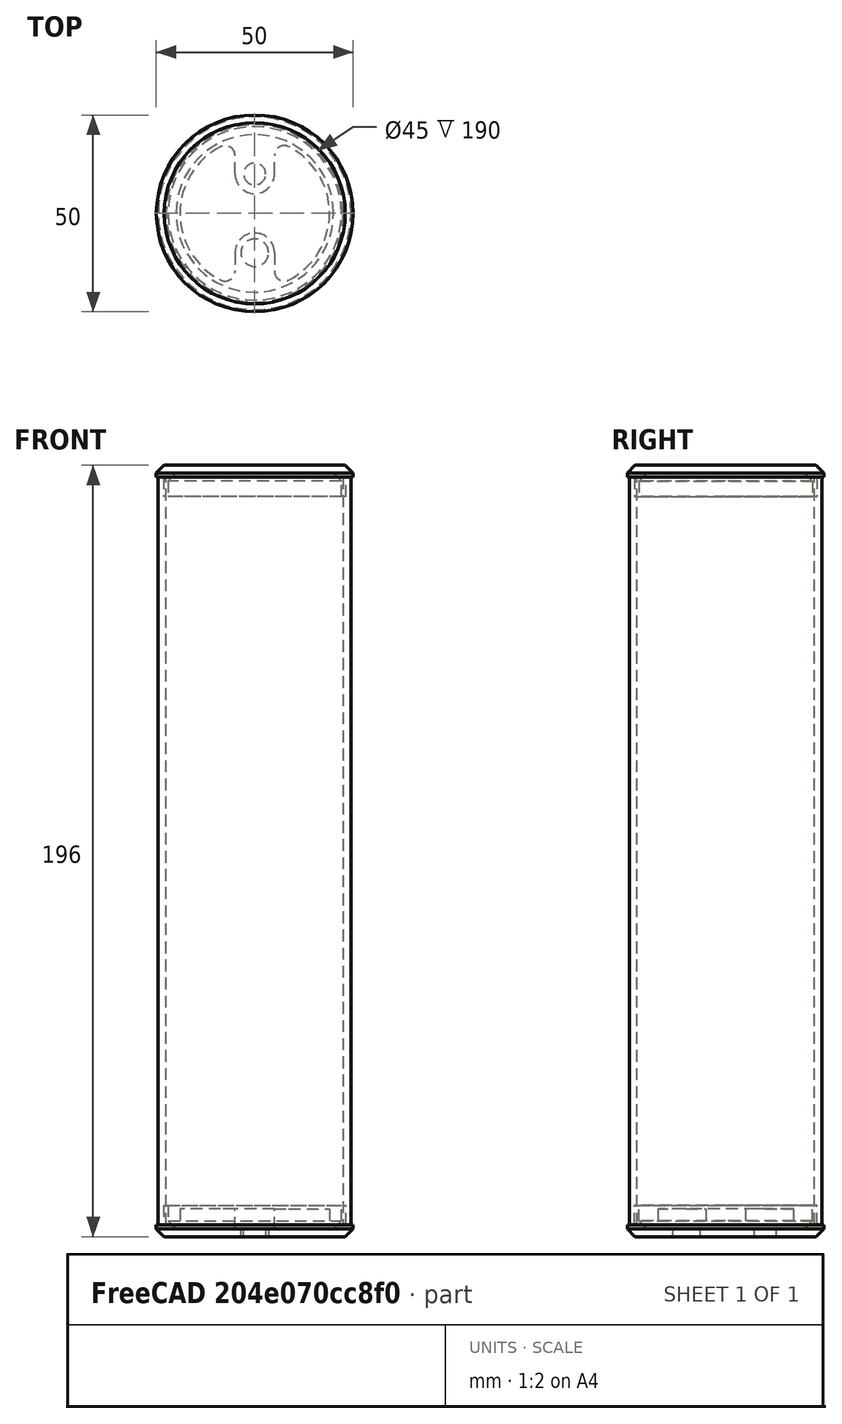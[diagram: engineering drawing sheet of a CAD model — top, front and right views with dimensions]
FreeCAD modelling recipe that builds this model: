
FCSTD DOCUMENT  (FreeCAD 0.19R14555 (Git shallow))
Label: hydrostatus_mockup
License: All rights reserved
LicenseURL: http://en.wikipedia.org/wiki/All_rights_reserved
objects: TechDraw::DrawViewDimension×13, Sketcher::SketchObject×9, PartDesign::Pad×6, TechDraw::DrawViewPart×6, PartDesign::Chamfer×4, PartDesign::Body×4, PartDesign::Pocket×3, Mesh::Feature×1, TechDraw::DrawSVGTemplate×1, TechDraw::DrawPage×1
note: 39 computed .brp shape members not serialized (recipe doc carries the construction recipe); baked Part::Feature solids carry a one-line shape summary decoded from their .brp

FEATURE [Sketcher::SketchObject] Sketch
  FullyConstrained = true
  MapMode = 5
  Support = -> [XY_Plane]
  sketch-geometry (1):
    g0: Circle CenterX=0 CenterY=0 CenterZ=0 NormalX=0 NormalY=0 NormalZ=1 AngleXU=0 Radius=23.15
  constraints (2):
    c: Coincident(g0,g-1)
    c: Diameter(g0) = 46.3
FEATURE [PartDesign::Pad] Pad
  Direction = (1,1,1)
  Length = 5
  Length2 = 100
  Profile = -> Sketch
  Type = 0
FEATURE [Sketcher::SketchObject] Sketch001
  FullyConstrained = true
  MapMode = 5
  Placement = pos=(0,0,5) rot=(0,0,1;0rad)
  Support = -> [Pad]
  sketch-geometry (1):
    g0: Circle CenterX=0 CenterY=0 CenterZ=0 NormalX=0 NormalY=0 NormalZ=1 AngleXU=0 Radius=25
  constraints (2):
    c: Coincident(g0,g-1)
    c: Diameter(g0) = 50
FEATURE [PartDesign::Pad] Pad001
  BaseFeature = -> Pad
  Direction = (1,1,1)
  Length = 3
  Length2 = 100
  Profile = -> Sketch001
  Type = 0
FEATURE [PartDesign::Chamfer] Chamfer
  Angle = 45
  Base = -> Pad001 [Edge3]
  BaseFeature = -> Pad001
  ChamferType = 0
  FlipDirection = false
  Size = 2
  Size2 = 1
  SupportTransform = false
FEATURE [Sketcher::SketchObject] Sketch002
  FullyConstrained = true
  MapMode = 5
  Placement = pos=(0,0,0) rot=(1,0,0;3.14159rad)
  Support = -> [Chamfer]
  sketch-geometry (1):
    g0: Circle CenterX=0 CenterY=0 CenterZ=0 NormalX=0 NormalY=0 NormalZ=1 AngleXU=0 Radius=22
  constraints (2):
    c: Coincident(g0,g-1)
    c: Diameter(g0) = 44
FEATURE [PartDesign::Pocket] Pocket
  BaseFeature = -> Chamfer
  Length = 6
  Length2 = 100
  Profile = -> Sketch002
  Type = 0
FEATURE [PartDesign::Chamfer] Chamfer001
  Angle = 45
  Base = -> Pocket [Edge11]
  BaseFeature = -> Pocket
  ChamferType = 0
  FlipDirection = false
  Size = 2
  Size2 = 1
  SupportTransform = false
FEATURE [PartDesign::Body] Body  label="hydrostatus_cap"
  Group = -> [Sketch,Pad,Sketch001,Pad001,Chamfer,Sketch002,Pocket,Chamfer001]
  Origin = -> Origin
  Placement = pos=(0,0,-15) rot=(0,0,1;0rad)
  Tip = -> Chamfer001
FEATURE [Sketcher::SketchObject] Sketch003
  FullyConstrained = true
  MapMode = 5
  Support = -> [XY_Plane001]
  sketch-geometry (1):
    g0: Circle CenterX=0 CenterY=0 CenterZ=0 NormalX=0 NormalY=0 NormalZ=1 AngleXU=0 Radius=23.15
  constraints (2):
    c: Coincident(g0,g-1)
    c: Diameter(g0) = 46.3
FEATURE [PartDesign::Pad] Pad002
  Direction = (1,1,1)
  Length = 5
  Length2 = 100
  Profile = -> Sketch003
  Type = 0
FEATURE [Sketcher::SketchObject] Sketch004
  FullyConstrained = true
  MapMode = 5
  Placement = pos=(0,0,5) rot=(0,0,1;0rad)
  Support = -> [Pad002]
  sketch-geometry (1):
    g0: Circle CenterX=0 CenterY=0 CenterZ=0 NormalX=0 NormalY=0 NormalZ=1 AngleXU=0 Radius=25
  constraints (2):
    c: Coincident(g0,g-1)
    c: Diameter(g0) = 50
FEATURE [PartDesign::Pad] Pad003
  BaseFeature = -> Pad002
  Direction = (1,1,1)
  Length = 3
  Length2 = 100
  Profile = -> Sketch004
  Type = 0
FEATURE [PartDesign::Chamfer] Chamfer002
  Angle = 45
  Base = -> Pad003 [Edge3]
  BaseFeature = -> Pad003
  ChamferType = 0
  FlipDirection = false
  Size = 2
  Size2 = 1
  SupportTransform = false
FEATURE [Sketcher::SketchObject] Sketch005
  FullyConstrained = true
  MapMode = 5
  Placement = pos=(0,0,0) rot=(1,0,0;3.14159rad)
  Support = -> [Chamfer002]
  sketch-geometry (1):
    g0: Circle CenterX=0 CenterY=0 CenterZ=0 NormalX=0 NormalY=0 NormalZ=1 AngleXU=0 Radius=22
  constraints (2):
    c: Coincident(g0,g-1)
    c: Diameter(g0) = 44
FEATURE [PartDesign::Pocket] Pocket001
  BaseFeature = -> Chamfer002
  Length = 6
  Length2 = 100
  Profile = -> Sketch005
  Type = 0
FEATURE [PartDesign::Chamfer] Chamfer003
  Angle = 45
  Base = -> Pocket001 [Edge11]
  BaseFeature = -> Pocket001
  ChamferType = 0
  FlipDirection = false
  Size = 2
  Size2 = 1
  SupportTransform = false
FEATURE [Sketcher::SketchObject] Sketch006
  FullyConstrained = true
  MapMode = 5
  Placement = pos=(0,0,8) rot=(0,0,1;0rad)
  Support = -> [Chamfer003]
  sketch-geometry (2):
    g0: Circle CenterX=0 CenterY=10 CenterZ=0 NormalX=0 NormalY=0 NormalZ=1 AngleXU=0 Radius=2.775
    g1: Circle CenterX=0 CenterY=-10 CenterZ=0 NormalX=0 NormalY=0 NormalZ=1 AngleXU=0 Radius=3.5
  constraints (6):
    c: PointOnObject(g0,g-2)
    c: Diameter(g0) = 5.55
    c: DistanceY(g-1,g0) = 10
    c: PointOnObject(g1,g-2)
    c: Diameter(g1) = 7
    c: DistanceY(g1,g-1) = 10
FEATURE [PartDesign::Pocket] Pocket002
  BaseFeature = -> Chamfer003
  Length = 5
  Length2 = 100
  Profile = -> Sketch006
  Type = 0
FEATURE [PartDesign::Body] Body001  label="hydrostatus_plug"
  Group = -> [Sketch003,Pad002,Sketch004,Pad003,Chamfer002,Sketch005,Pocket001,Chamfer003,Sketch006,Pocket002]
  Origin = -> Origin001
  Placement = pos=(-1.7e-14,-1.7e-14,-195) rot=(0,1,0;3.14159rad)
  Tip = -> Pocket002
FEATURE [Sketcher::SketchObject] Sketch007
  FullyConstrained = true
  MapMode = 5
  Support = -> [XY_Plane002]
  sketch-geometry (2):
    g0: Circle CenterX=0 CenterY=0 CenterZ=0 NormalX=0 NormalY=0 NormalZ=1 AngleXU=0 Radius=24.5
    g1: Circle CenterX=0 CenterY=0 CenterZ=0 NormalX=0 NormalY=0 NormalZ=1 AngleXU=0 Radius=22.5
  constraints (4):
    c: Coincident(g0,g-1)
    c: Coincident(g1,g0)
    c: Diameter(g1) = 45
    c: Diameter(g0) = 49
FEATURE [PartDesign::Pad] Pad004
  Direction = (1,1,1)
  Length = 190
  Length2 = 100
  Profile = -> Sketch007
  Reversed = true
  Type = 0
FEATURE [PartDesign::Body] Body002  label="hydrostatus_tube"
  Group = -> [Sketch007,Pad004]
  Origin = -> Origin002
  Placement = pos=(0,0,-10) rot=(0,0,1;0rad)
  Tip = -> Pad004
FEATURE [Mesh::Feature] prototype_layout_refined
  Placement = pos=(-0.7,10,-54) rot=(-1,0,0;4.71239rad)
FEATURE [Sketcher::SketchObject] Sketch008
  FullyConstrained = true
  MapMode = 5
  Support = -> [XY_Plane003]
  sketch-geometry (12):
    g0: ArcOfCircle CenterX=0 CenterY=0 CenterZ=0 NormalX=0 NormalY=0 NormalZ=1 AngleXU=0 Radius=19 StartAngle=2.04266 EndAngle=4.24053
    g1: ArcOfCircle CenterX=0 CenterY=10 CenterZ=0 NormalX=0 NormalY=0 NormalZ=1 AngleXU=0 Radius=5 StartAngle=3.14159 EndAngle=6.28319
    g2: LineSegment StartX=5 StartY=10 StartZ=0 EndX=5 EndY=14.6969 EndZ=0
    g3: LineSegment StartX=-5 StartY=10 StartZ=0 EndX=-5 EndY=14.6969 EndZ=0
    g4: ArcOfCircle CenterX=0 CenterY=-10 CenterZ=0 NormalX=0 NormalY=0 NormalZ=1 AngleXU=0 Radius=5 StartAngle=2e-16 EndAngle=3.14159
    g5: LineSegment StartX=-5 StartY=-10 StartZ=0 EndX=-5 EndY=-14.6969 EndZ=0
    g6: LineSegment StartX=5 StartY=-10 StartZ=0 EndX=5 EndY=-14.6969 EndZ=0
    g7: ArcOfCircle CenterX=0 CenterY=0 CenterZ=0 NormalX=0 NormalY=0 NormalZ=1 AngleXU=0 Radius=19 StartAngle=5.18425 EndAngle=7.38212
    g8: ArcOfCircle CenterX=7.5 CenterY=-14.6969 CenterZ=0 NormalX=0 NormalY=0 NormalZ=1 AngleXU=0 Radius=2.5 StartAngle=3.14159 EndAngle=5.18425
    g9: ArcOfCircle CenterX=-7.5 CenterY=-14.6969 CenterZ=0 NormalX=0 NormalY=0 NormalZ=1 AngleXU=0 Radius=2.5 StartAngle=4.24053 EndAngle=6.28319
    g10: ArcOfCircle CenterX=7.5 CenterY=14.6969 CenterZ=0 NormalX=0 NormalY=0 NormalZ=1 AngleXU=0 Radius=2.5 StartAngle=1.09893 EndAngle=3.14159
    g11: ArcOfCircle CenterX=-7.5 CenterY=14.6969 CenterZ=0 NormalX=0 NormalY=0 NormalZ=1 AngleXU=0 Radius=2.5 StartAngle=1e-16 EndAngle=2.04266
  constraints (30):
    c: Coincident(g0,g-1)
    c: Diameter(g0) = 38
    c: Tangent(g1,g3) = 1.5708
    c: Tangent(g1,g2) = -1.5708
    c: Vertical(g2)
    c: PointOnObject(g1,g-2)
    c: Tangent(g4,g6) = 1.5708
    c: Tangent(g4,g5) = -1.5708
    c: Vertical(g5)
    c: PointOnObject(g4,g-2)
    c: Diameter(g4) = 10
    c: Diameter(g1) = 10
    c: Parallel(g5,g6)
    c: Parallel(g2,g3)
    c: DistanceY(g4) = -10
    c: DistanceY(g1) = 10
    c: Equal(g0,g7)
    c: Coincident(g0,g7)
    c: Tangent(g6,g8) = -1.5708
    c: Tangent(g7,g8) = -1.5708
    c: Tangent(g5,g9) = 1.5708
    c: Tangent(g0,g9) = -1.5708
    c: Diameter(g8) = 5
    c: Diameter(g9) = 5
    c: Tangent(g2,g10) = 1.5708
    c: Tangent(g7,g10) = -1.5708
    c: Tangent(g3,g11) = -1.5708
    c: Tangent(g0,g11) = -1.5708
    c: Diameter(g11) = 5
    c: Diameter(g10) = 5
FEATURE [PartDesign::Pad] Pad005
  Direction = (1,1,1)
  Length = 5
  Length2 = 100
  Profile = -> Sketch008
  Type = 0
FEATURE [PartDesign::Body] Body003  label="hydrostatus_electronics"
  Group = -> [Sketch008,Pad005]
  Origin = -> Origin003
  Placement = pos=(0,0,-201) rot=(0,0,1;0rad)
  Tip = -> Pad005
FEATURE [TechDraw::DrawSVGTemplate] Template
  Height = 210
  Orientation = 1
  Width = 297
FEATURE [TechDraw::DrawViewPart] View  label="cap 45*d profile"
  CoarseView = false
  Direction = (0,0,-1)
  Focus = 100
  HardHidden = false
  IsoCount = 0
  IsoHidden = false
  IsoVisible = false
  LockPosition = false
  Perspective = false
  Rotation = 0
  ScaleType = 0
  SeamHidden = false
  SeamVisible = true
  SmoothHidden = false
  SmoothVisible = true
  Source = -> [Body]
  X = 40.3062
  XDirection = (1,0,0)
  Y = 119.923
FEATURE [TechDraw::DrawViewPart] View001  label="cap bottom profile"
  CoarseView = false
  Direction = (0,-0.707,-0.707)
  Focus = 100
  HardHidden = false
  IsoCount = 0
  IsoHidden = false
  IsoVisible = false
  LockPosition = false
  Perspective = false
  Rotation = 0
  ScaleType = 0
  SeamHidden = false
  SeamVisible = true
  SmoothHidden = false
  SmoothVisible = true
  Source = -> [Body]
  X = 39.967
  XDirection = (1,0,0)
  Y = 175.886
FEATURE [TechDraw::DrawViewPart] View002  label="cap side profile"
  CoarseView = false
  Direction = (0,-1,0)
  Focus = 100
  HardHidden = false
  IsoCount = 0
  IsoHidden = false
  IsoVisible = false
  LockPosition = false
  Perspective = false
  Rotation = 0
  ScaleType = 0
  SeamHidden = false
  SeamVisible = true
  SmoothHidden = false
  SmoothVisible = true
  Source = -> [Body]
  X = 40.3062
  XDirection = (1,0,0)
  Y = 79.2234
FEATURE [TechDraw::DrawViewPart] View003  label="plug side profile"
  CoarseView = false
  Direction = (0,-1,0)
  Focus = 100
  HardHidden = false
  IsoCount = 0
  IsoHidden = false
  IsoVisible = false
  LockPosition = false
  Perspective = false
  Rotation = 0
  ScaleType = 0
  SeamHidden = false
  SeamVisible = true
  SmoothHidden = false
  SmoothVisible = true
  Source = -> [Body001]
  X = 100.452
  XDirection = (1,0,0)
  Y = 79.0904
FEATURE [TechDraw::DrawViewPart] View004  label="plug 45*d profile"
  CoarseView = false
  Direction = (0,0.707,0.707)
  Focus = 100
  HardHidden = false
  IsoCount = 0
  IsoHidden = false
  IsoVisible = false
  LockPosition = false
  Perspective = false
  Rotation = 0
  ScaleType = 0
  SeamHidden = false
  SeamVisible = true
  SmoothHidden = false
  SmoothVisible = true
  Source = -> [Body001]
  X = 100.216
  XDirection = (1,0,0)
  Y = 176.366
FEATURE [TechDraw::DrawViewPart] View005  label="plug bottom profile"
  CoarseView = false
  Direction = (0,0,1)
  Focus = 100
  HardHidden = false
  IsoCount = 0
  IsoHidden = false
  IsoVisible = false
  LockPosition = false
  Perspective = false
  Rotation = 0
  ScaleType = 0
  SeamHidden = false
  SeamVisible = true
  SmoothHidden = false
  SmoothVisible = true
  Source = -> [Body001]
  X = 100.216
  XDirection = (1,0,0)
  Y = 120.074
FEATURE [TechDraw::DrawViewDimension] Dimension
  Arbitrary = false
  ArbitraryTolerances = false
  EqualTolerance = true
  FormatSpec = ⌀%.2f
  FormatSpecOverTolerance = %+.2f
  FormatSpecUnderTolerance = %+.2f
  Inverted = false
  LockPosition = false
  MeasureType = 1
  OverTolerance = 0
  References2D = -> [View005]
  Rotation = 0
  ScaleType = 0
  TheoreticalExact = false
  Type = 5
  UnderTolerance = 0
  X = 20.4127
  Y = 23.1606
FEATURE [TechDraw::DrawViewDimension] Dimension001
  Arbitrary = false
  ArbitraryTolerances = false
  EqualTolerance = true
  FormatSpec = ⌀%.2f
  FormatSpecOverTolerance = %+.2f
  FormatSpecUnderTolerance = %+.2f
  Inverted = false
  LockPosition = false
  MeasureType = 1
  OverTolerance = 0
  References2D = -> [View005]
  Rotation = 0
  ScaleType = 0
  TheoreticalExact = false
  Type = 5
  UnderTolerance = 0
  X = -10.9915
  Y = 3.92553
FEATURE [TechDraw::DrawViewDimension] Dimension002
  Arbitrary = false
  ArbitraryTolerances = false
  EqualTolerance = true
  FormatSpec = ⌀%.2f
  FormatSpecOverTolerance = %+.2f
  FormatSpecUnderTolerance = %+.2f
  Inverted = false
  LockPosition = false
  MeasureType = 1
  OverTolerance = 0
  References2D = -> [View005]
  Rotation = 0
  ScaleType = 0
  TheoreticalExact = false
  Type = 5
  UnderTolerance = 0
  X = 7.06595
  Y = 1.37393
FEATURE [TechDraw::DrawViewDimension] Dimension003
  Arbitrary = false
  ArbitraryTolerances = false
  EqualTolerance = true
  FormatSpec = %.2f
  FormatSpecOverTolerance = %+.2f
  FormatSpecUnderTolerance = %+.2f
  Inverted = false
  LockPosition = false
  MeasureType = 1
  OverTolerance = 0
  References2D = -> [View005]
  Rotation = 0
  ScaleType = 0
  TheoreticalExact = false
  Type = 1
  UnderTolerance = 0
  X = -30.0989
  Y = 3.43484
FEATURE [TechDraw::DrawViewDimension] Dimension004
  Arbitrary = false
  ArbitraryTolerances = false
  EqualTolerance = true
  FormatSpec = %.2f
  FormatSpecOverTolerance = %+.2f
  FormatSpecUnderTolerance = %+.2f
  Inverted = false
  LockPosition = false
  MeasureType = 1
  OverTolerance = 0
  References2D = -> [View005]
  Rotation = 0
  ScaleType = 0
  TheoreticalExact = false
  Type = 0
  UnderTolerance = 0
  X = -29.7997
  Y = -5.56116
FEATURE [TechDraw::DrawViewDimension] Dimension005
  Arbitrary = false
  ArbitraryTolerances = false
  EqualTolerance = true
  FormatSpec = %.2f
  FormatSpecOverTolerance = %+.2f
  FormatSpecUnderTolerance = %+.2f
  Inverted = false
  LockPosition = false
  MeasureType = 1
  OverTolerance = 0
  References2D = -> [View005]
  Rotation = 0
  ScaleType = 0
  TheoreticalExact = false
  Type = 2
  UnderTolerance = 0
  X = 23.809
  Y = -25.4331
FEATURE [TechDraw::DrawViewDimension] Dimension006
  Arbitrary = false
  ArbitraryTolerances = false
  EqualTolerance = true
  FormatSpec = %.2f
  FormatSpecOverTolerance = %+.2f
  FormatSpecUnderTolerance = %+.2f
  Inverted = false
  LockPosition = false
  MeasureType = 1
  OverTolerance = 0
  References2D = -> [View005]
  Rotation = 0
  ScaleType = 0
  TheoreticalExact = false
  Type = 2
  UnderTolerance = 0
  X = -27.6228
  Y = 24.4504
FEATURE [TechDraw::DrawViewDimension] Dimension007
  Arbitrary = false
  ArbitraryTolerances = false
  EqualTolerance = true
  FormatSpec = %.2f
  FormatSpecOverTolerance = %+.2f
  FormatSpecUnderTolerance = %+.2f
  Inverted = false
  LockPosition = false
  MeasureType = 1
  OverTolerance = 0
  References2D = -> [View003]
  Rotation = 0
  ScaleType = 0
  TheoreticalExact = false
  Type = 2
  UnderTolerance = 0
  X = 24.6487
  Y = -6.15127
FEATURE [TechDraw::DrawViewDimension] Dimension008
  Arbitrary = false
  ArbitraryTolerances = false
  EqualTolerance = true
  FormatSpec = %.2f
  FormatSpecOverTolerance = %+.2f
  FormatSpecUnderTolerance = %+.2f
  Inverted = false
  LockPosition = false
  MeasureType = 1
  OverTolerance = 0
  References2D = -> [View003]
  Rotation = 0
  ScaleType = 0
  TheoreticalExact = false
  Type = 2
  UnderTolerance = 0
  X = -29.2968
  Y = -1.02543
FEATURE [TechDraw::DrawViewDimension] Dimension009
  Arbitrary = false
  ArbitraryTolerances = false
  EqualTolerance = true
  FormatSpec = %.2f
  FormatSpecOverTolerance = %+.2f
  FormatSpecUnderTolerance = %+.2f
  Inverted = false
  LockPosition = false
  MeasureType = 1
  OverTolerance = 0
  References2D = -> [View003]
  Rotation = 0
  ScaleType = 0
  TheoreticalExact = false
  Type = 1
  UnderTolerance = 0
  X = -0.552153
  Y = -10.547
FEATURE [TechDraw::DrawViewDimension] Dimension010
  Arbitrary = false
  ArbitraryTolerances = false
  EqualTolerance = true
  FormatSpec = %.2f
  FormatSpecOverTolerance = %+.2f
  FormatSpecUnderTolerance = %+.2f
  Inverted = false
  LockPosition = false
  MeasureType = 1
  OverTolerance = 0
  References2D = -> [View003]
  Rotation = 0
  ScaleType = 0
  TheoreticalExact = false
  Type = 1
  UnderTolerance = 0
  X = -0.315516
  Y = 9.44266
FEATURE [TechDraw::DrawViewDimension] Dimension011
  Arbitrary = false
  ArbitraryTolerances = false
  EqualTolerance = true
  FormatSpec = ⌀%.2f
  FormatSpecOverTolerance = %+.2f
  FormatSpecUnderTolerance = %+.2f
  Inverted = false
  LockPosition = false
  MeasureType = 1
  OverTolerance = 0
  References2D = -> [View005]
  Rotation = 0
  ScaleType = 0
  TheoreticalExact = false
  Type = 5
  UnderTolerance = 0
  X = 24.8753
  Y = 19.3096
FEATURE [TechDraw::DrawViewDimension] Dimension012
  Arbitrary = false
  ArbitraryTolerances = false
  EqualTolerance = true
  FormatSpec = ⌀%.2f
  FormatSpecOverTolerance = %+.2f
  FormatSpecUnderTolerance = %+.2f
  Inverted = false
  LockPosition = false
  MeasureType = 1
  OverTolerance = 0
  References2D = -> [View005]
  Rotation = 0
  ScaleType = 0
  TheoreticalExact = false
  Type = 5
  UnderTolerance = 0
  X = 28.6182
  Y = 14.3091
FEATURE [TechDraw::DrawPage] Page001  label="Technical Drawing"
  KeepUpdated = true
  NextBalloonIndex = 1
  ProjectionType = 0
  Template = -> Template
  Views = -> [View,View001,View002,View003,View004,View005,Dimension,Dimension001,Dimension002,Dimension003,Dimension004,Dimension005,Dimension006,Dimension007,Dimension008,Dimension009,Dimension010,Dimension011,Dimension012]
